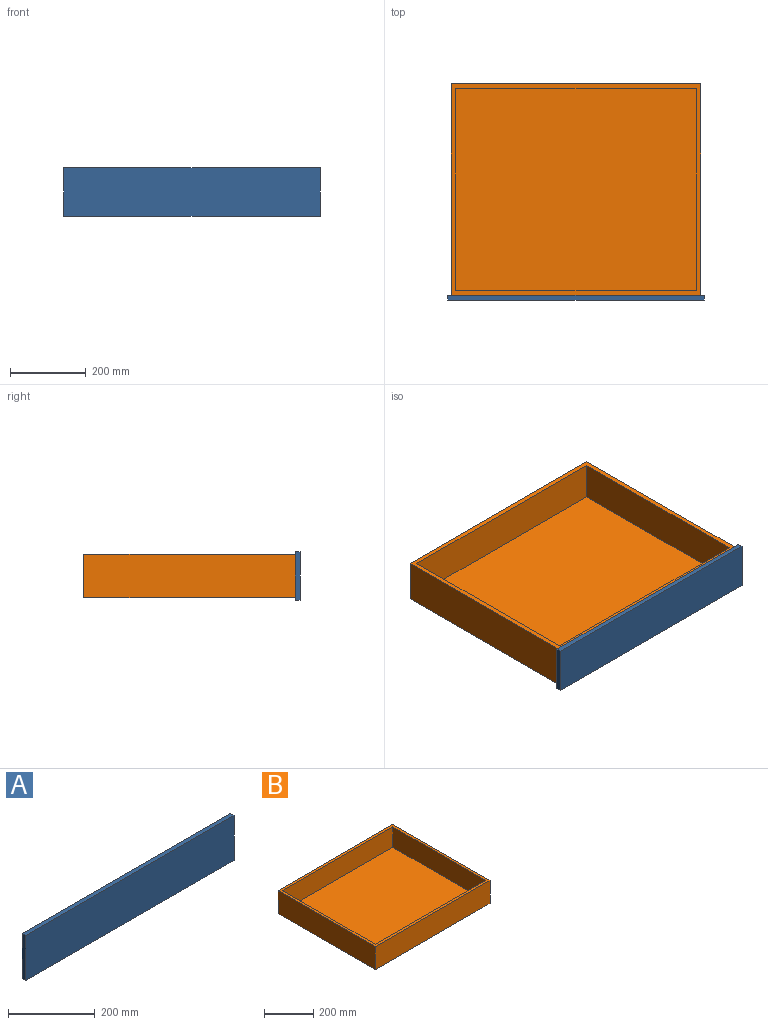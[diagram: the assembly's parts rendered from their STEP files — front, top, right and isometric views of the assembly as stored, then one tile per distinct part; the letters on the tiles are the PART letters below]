
ASSEMBLY  parts=2 mates=1
PART A: 6 faces, bbox 679.5x12.7x127 mm
  f0: plane 679.45x12.7mm, normal (0,0,1), area 8629mm2, adj f1,f3,f4,f5
  f1: plane 127x12.7mm, normal (-1,0,0), area 1612.9mm2, adj f0,f2,f4,f5
  f2: plane 679.45x12.7mm, normal (0,0,-1), area 8629mm2, adj f1,f3,f4,f5
  f3: plane 127x12.7mm, normal (1,0,0), area 1612.9mm2, adj f0,f2,f4,f5
  f4: plane 679.45x127mm, normal (0,-1,0), area 86290.1mm2, adj f0,f1,f2,f3
  f5: plane 679.45x127mm, normal (0,1,0), area 86290.1mm2, adj f0,f1,f2,f3
PART B: 11 faces, bbox 660.4x558.8x114.3 mm
  f0: plane 660.4x114.3mm, normal (0,1,0), area 75483.7mm2, adj f1,f3,f4,f5
  f1: plane 558.8x114.3mm, normal (-1,0,0), area 63870.8mm2, adj f0,f2,f4,f5
  f2: plane 660.4x114.3mm, normal (0,-1,0), area 75483.7mm2, adj f1,f3,f4,f5
  f3: plane 558.8x114.3mm, normal (1,0,0), area 63870.8mm2, adj f0,f2,f4,f5
  f4: plane 660.4x558.8mm, normal (0,0,1), area 30322.5mm2, adj f0,f1,f2,f3,f6,f7,f8,f9
  f5: plane 660.4x558.8mm, normal (0,0,-1), area 369031.5mm2, adj f0,f1,f2,f3
  f6: plane 635x101.6mm, normal (0,-1,0), area 64516mm2, adj f4,f7,f9,f10
  f7: plane 533.4x101.6mm, normal (1,0,0), area 54193.4mm2, adj f4,f6,f8,f10
  f8: plane 635x101.6mm, normal (0,1,0), area 64516mm2, adj f4,f7,f9,f10
  f9: plane 533.4x101.6mm, normal (-1,0,0), area 54193.4mm2, adj f4,f6,f8,f10
  f10: plane 635x533.4mm, normal (0,0,1), area 338709mm2, adj f6,f7,f8,f9
PLACE A t=(175.8,-285.13,-167.51)mm
PLACE B t=(175.8,0.62,-167.51)mm
MATE fastened A.f5 <-> B.f2  axis (0,1,0) through (175.8,-278.78,-167.51)mm
